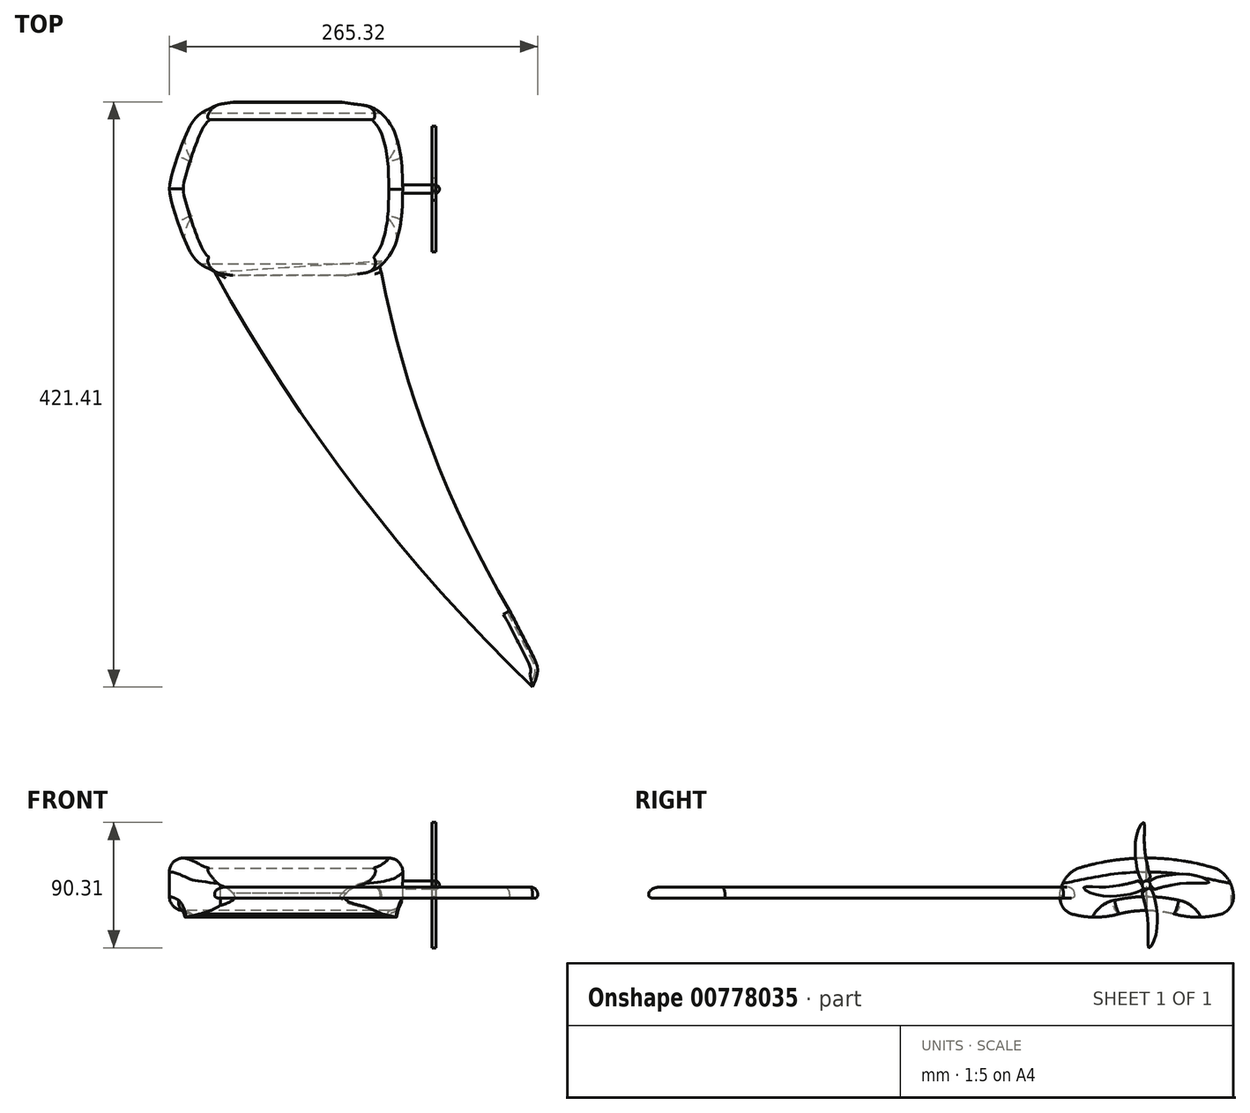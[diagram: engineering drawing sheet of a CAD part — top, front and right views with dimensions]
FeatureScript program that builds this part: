
annotation { "Feature Type Name" : "Feature", "Feature Type Description" : "" }
export const myFeature = defineFeature(function(context is Context, id is Id, definition is map)
    precondition{}
    {
        {
            var Q0;
            Q0=qCreatedBy(makeId("Right.planeOp"),FACE);
            var sketch = newSketch(context, id + "F0", { "sketchPlane" : qUnion([Q0])});
            skArc(sketch, "E0", {"start": v(50, -7.54) * mm, "mid": v(0, 0.01) * mm, "end": v(-50, -7.54) * mm});
            skArc(sketch, "E1", {"start": v(-50, -7.54) * mm, "mid": v(-58.49, -14.8) * mm, "end": v(-62.37, -25.27) * mm});
            skArc(sketch, "E2", {"start": v(-62.37, -25.27) * mm, "mid": v(-61.02, -34.16) * mm, "end": v(-54.32, -40.16) * mm});
            skArc(sketch, "E3", {"start": v(-54.32, -40.16) * mm, "mid": v(-36.95, -42.59) * mm, "end": v(-19.58, -40.16) * mm});
            skArc(sketch, "E4.MirrorCS", {"start": v(54.33, -40.16) * mm, "mid": v(36.96, -42.6) * mm, "end": v(19.6, -40.16) * mm});
            skArc(sketch, "E5.MirrorCS", {"start": v(62.37, -25.28) * mm, "mid": v(61.03, -34.17) * mm, "end": v(54.33, -40.16) * mm});
            skArc(sketch, "E6.MirrorCS", {"start": v(50, -7.55) * mm, "mid": v(58.5, -14.8) * mm, "end": v(62.37, -25.28) * mm});
            skFitSpline(sketch, "E7", {"points": [v(50, -7.55) * mm, v(50, -7.54) * mm], "startDerivative": vector(0, 0) * mm, "endDerivative": vector(0, 0) * mm});
            skArc(sketch, "E8", {"start": v(19.6, -40.16) * mm, "mid": v(0, -37.76) * mm, "end": v(-19.58, -40.16) * mm});
            skSolve(sketch);
        }
        {
            var Q0;
            Q0 = qSketchRegion(id + "F0", true);
            extrude(context, id + "F1", {"entities" : qUnion([Q0]), "depth" : 200 * mm, "offsetDistance" : 25 * mm});
        }
        {
            var Q0;
            Q0=qCreatedBy(makeId("Top.planeOp"),FACE);
            var sketch = newSketch(context, id + "F2", { "sketchPlane" : qUnion([Q0])});
            skFitSpline(sketch, "E9", {"points": [v(40.59, -61.05) * mm, v(32.26, -57.57) * mm, v(26.13, -54.16) * mm, v(20.46, -48.17) * mm, v(16.4, -40.56) * mm, v(11.23, -27.6) * mm, v(7.18, -15.78) * mm, v(3.78, 0) * mm], "startDerivative": vector(-74.7, 20.3) * mm, "endDerivative": vector(-2.34, 92.01) * mm});
            skFitSpline(sketch, "E10", {"points": [v(40.59, -61.05) * mm, v(44.6, -61.62) * mm, v(50.35, -62.52) * mm, v(55.66, -63.27) * mm], "startDerivative": vector(14.16, -1.62) * mm, "endDerivative": vector(15.47, -2.1) * mm});
            skFitSpline(sketch, "E11.MirrorCS", {"points": [v(40.59, 61.05) * mm, v(44.6, 61.62) * mm, v(50.35, 62.52) * mm, v(55.66, 63.27) * mm], "startDerivative": vector(14.16, 1.62) * mm, "endDerivative": vector(15.47, 2.1) * mm});
            skFitSpline(sketch, "E12", {"points": [v(139.37, 60.82) * mm, v(146.45, 59.7) * mm, v(152.68, 57.14) * mm, v(157.64, 53.32) * mm, v(162.03, 47.94) * mm, v(165.29, 42.55) * mm, v(168.26, 34.2) * mm, v(170.1, 25.98) * mm, v(171.23, 17.63) * mm, v(171.66, 9.98) * mm, v(171.94, -0.22) * mm], "startDerivative": vector(74.25, -8.33) * mm, "endDerivative": vector(2.34, -92.01) * mm});
            skFitSpline(sketch, "E13", {"points": [v(139.37, 60.82) * mm, v(134.8, 61.4) * mm, v(129.04, 62.3) * mm, v(123.73, 63.05) * mm], "startDerivative": vector(-14.16, 1.62) * mm, "endDerivative": vector(-15.47, 2.1) * mm});
            skFitSpline(sketch, "E14.MirrorCS", {"points": [v(139.37, -61.27) * mm, v(146.45, -60.14) * mm, v(152.68, -57.59) * mm, v(157.64, -53.76) * mm, v(162.03, -48.38) * mm, v(165.29, -43) * mm, v(168.26, -34.64) * mm, v(170.1, -26.43) * mm, v(171.23, -18.07) * mm, v(171.66, -10.42) * mm, v(171.94, -0.22) * mm], "startDerivative": vector(74.25, 8.33) * mm, "endDerivative": vector(2.34, 92.01) * mm});
            skFitSpline(sketch, "E15.MirrorCS", {"points": [v(139.37, -61.27) * mm, v(134.8, -61.84) * mm, v(129.04, -62.74) * mm, v(123.73, -63.5) * mm], "startDerivative": vector(-14.16, -1.62) * mm, "endDerivative": vector(-15.47, -2.1) * mm});
            skLineSegment(sketch, "E16", {"start": v(149.22, -63.5) * mm, "end": v(166.17, -79.7) * mm});
            skLineSegment(sketch, "E17", {"start": v(166.17, -79.7) * mm, "end": v(210.3, -72.3) * mm});
            skLineSegment(sketch, "E18", {"start": v(210.3, -72.3) * mm, "end": v(219.4, 8.55) * mm});
            skLineSegment(sketch, "E19", {"start": v(219.4, 8.55) * mm, "end": v(210.3, 73.23) * mm});
            skLineSegment(sketch, "E20", {"start": v(210.3, 73.23) * mm, "end": v(164.49, 80.64) * mm});
            skLineSegment(sketch, "E21", {"start": v(149.22, 63.05) * mm, "end": v(164.49, 80.64) * mm});
            skLineSegment(sketch, "E22", {"start": v(55.66, 63.27) * mm, "end": v(33.8, 74.16) * mm});
            skLineSegment(sketch, "E23", {"start": v(33.8, 74.16) * mm, "end": v(-5.06, 70.36) * mm});
            skLineSegment(sketch, "E24", {"start": v(-5.06, 70.36) * mm, "end": v(-13.47, 35.5) * mm});
            skLineSegment(sketch, "E25", {"start": v(-13.47, 35.5) * mm, "end": v(-13.27, -25.39) * mm});
            skLineSegment(sketch, "E26", {"start": v(-13.27, -25.39) * mm, "end": v(-7.26, -54.23) * mm});
            skLineSegment(sketch, "E27", {"start": v(-7.26, -54.23) * mm, "end": v(-1.45, -73.86) * mm});
            skLineSegment(sketch, "E28", {"start": v(-1.45, -73.86) * mm, "end": v(53.23, -68.45) * mm});
            skLineSegment(sketch, "E29", {"start": v(53.23, -68.45) * mm, "end": v(55.66, -63.27) * mm});
            skFitSpline(sketch, "E30.MirrorCS", {"points": [v(40.59, 61.05) * mm, v(32.26, 57.57) * mm, v(26.13, 54.16) * mm, v(20.46, 48.17) * mm, v(16.4, 40.56) * mm, v(11.23, 27.6) * mm, v(7.18, 15.78) * mm, v(3.78, 0) * mm], "startDerivative": vector(-74.7, -20.3) * mm, "endDerivative": vector(-2.34, -92.01) * mm});
            skLineSegment(sketch, "E31", {"start": v(149.22, -63.5) * mm, "end": v(123.73, -63.5) * mm});
            skLineSegment(sketch, "E32", {"start": v(123.73, 63.05) * mm, "end": v(149.22, 63.05) * mm});
            skSolve(sketch);
        }
        {
            var Q0;
            Q0=makeQuery(id+"F2.imprint","IMPRINT",FACE,{"disambiguationData":[TD([[makeQuery(id+"F2.imprint","IMPRINT",EDGE,{"derivedFrom":sQuery(id+"F2.wireOp",EDGE,"E9")}),1.0]])]});
            var Q1;
            Q1=makeQuery(id+"F2.imprint","IMPRINT",FACE,{"disambiguationData":[TD([[makeQuery(id+"F2.imprint","IMPRINT",EDGE,{"derivedFrom":sQuery(id+"F2.wireOp",EDGE,"E12")}),1.0]])]});
            extrude(context, id + "F3", {"entities" : qUnion([Q0, Q1]), "operationType" : NewBodyOperationType.REMOVE, "oppositeDirection" : true, "depth" : 74 * mm, "offsetDistance" : 25 * mm});
        }
        {
            var Q0;
            Q0=makeQuery(id+"F1.opExtrude","SWEPT_FACE",FACE,{"disambiguationData":[OSD([sQuery(id+"F0.wireOp",EDGE,"E0")])]});
            var Q1;
            Q1=makeQuery(id+"F1.opExtrude","SWEPT_FACE",FACE,{"disambiguationData":[OSD([sQuery(id+"F0.wireOp",EDGE,"E8")])]});
            fillet(context, id + "F4", {"entities" : qUnion([Q0, Q1]), "radius" : 10 * mm, "tangentPropagation" : true, "allowEdgeOverflow" : false});
        }
        {
            var Q0;
            Q0=qCreatedBy(makeId("Top.planeOp"),FACE);
            var sketch = newSketch(context, id + "F5", { "sketchPlane" : qUnion([Q0])});
            skArc(sketch, "E33", {"start": v(23.4, -59.92) * mm, "mid": v(126.63, -218) * mm, "end": v(252.43, -358.78) * mm});
            skArc(sketch, "E34", {"start": v(143.47, -59.92) * mm, "mid": v(179.26, -185.83) * mm, "end": v(235.94, -303.81) * mm});
            skFitSpline(sketch, "E35", {"points": [v(235.94, -303.81) * mm, v(251.98, -334.96) * mm, v(256.1, -346.87) * mm, v(252.43, -358.78) * mm], "startDerivative": vector(39.46, -76.57) * mm, "endDerivative": vector(-19.99, -45.14) * mm});
            skArc(sketch, "E36.MirrorCS", {"start": v(23.4, 59.92) * mm, "mid": v(126.63, 218) * mm, "end": v(252.43, 358.78) * mm});
            skArc(sketch, "E37.MirrorCS", {"start": v(143.47, 59.92) * mm, "mid": v(179.26, 185.83) * mm, "end": v(235.94, 303.81) * mm});
            skFitSpline(sketch, "E38.MirrorCS", {"points": [v(235.94, 303.81) * mm, v(251.98, 334.96) * mm, v(256.1, 346.87) * mm, v(252.43, 358.78) * mm], "startDerivative": vector(39.46, 76.57) * mm, "endDerivative": vector(-19.99, 45.14) * mm});
            skArc(sketch, "E39", {"start": v(143.47, -51.87) * mm, "mid": v(142.63, -55.9) * mm, "end": v(143.47, -59.92) * mm});
            skLineSegment(sketch, "E40", {"start": v(23.4, -59.92) * mm, "end": v(143.47, -51.87) * mm});
            skLineSegment(sketch, "E41.MirrorCS", {"start": v(23.4, 59.92) * mm, "end": v(143.47, 51.87) * mm});
            skArc(sketch, "E42.MirrorCS", {"start": v(143.47, 51.87) * mm, "mid": v(142.63, 55.9) * mm, "end": v(143.47, 59.92) * mm});
            skSolve(sketch);
        }
        {
            var Q0;
            Q0=makeQuery(id+"F5.imprint","IMPRINT",FACE,{"disambiguationData":[TD([[makeQuery(id+"F5.imprint","IMPRINT",EDGE,{"derivedFrom":sQuery(id+"F5.wireOp",EDGE,"E33")}),1.0]])]});
            var Q1;
            Q1=makeQuery(id+"F5.imprint","IMPRINT",FACE,{"disambiguationData":[TD([[makeQuery(id+"F5.imprint","IMPRINT",EDGE,{"derivedFrom":sQuery(id+"F5.wireOp",EDGE,"E36.MirrorCS")}),-1.0]])]});
            extrude(context, id + "F6", {"entities" : qUnion([Q0, Q1]), "depth" : 8 * mm, "offsetDistance" : 25 * mm});
        }
        {
            var Q0;
            Q0=makeQuery(id+"F6.opExtrude","CAP_FACE",FACE,{"disambiguationData":[OSD([sQuery(id+"F5.wireOp",EDGE,"6FdpHKt3-hqUe-cJeI-kYoZ-nh7BHDurZMUy"),sQuery(id+"F5.wireOp",EDGE,"E33"),sQuery(id+"F5.wireOp",EDGE,"E34"),sQuery(id+"F5.wireOp",EDGE,"E35")])],"isStart":false});
            var Q1;
            Q1=makeQuery(id+"F6.opExtrude","CAP_FACE",FACE,{"disambiguationData":[OSD([sQuery(id+"F5.wireOp",EDGE,"E36.MirrorCS"),sQuery(id+"F5.wireOp",EDGE,"b9c2965b-7b99-427b-b453-79c65aef091a0.MirrorCS"),sQuery(id+"F5.wireOp",EDGE,"E37.MirrorCS"),sQuery(id+"F5.wireOp",EDGE,"E38.MirrorCS")])],"isStart":false});
            fillet(context, id + "F7", {"entities" : qUnion([Q0, Q1]), "radius" : 5 * mm, "tangentPropagation" : true, "allowEdgeOverflow" : false});
        }
        {
            var Q0;
            Q0=makeQuery(id+"F6.opExtrude","CAP_FACE",FACE,{"disambiguationData":[OSD([sQuery(id+"F5.wireOp",EDGE,"E36.MirrorCS"),sQuery(id+"F5.wireOp",EDGE,"b9c2965b-7b99-427b-b453-79c65aef091a0.MirrorCS"),sQuery(id+"F5.wireOp",EDGE,"E37.MirrorCS"),sQuery(id+"F5.wireOp",EDGE,"E38.MirrorCS")])],"isStart":true});
            var Q1;
            Q1=makeQuery(id+"F6.opExtrude","CAP_FACE",FACE,{"disambiguationData":[OSD([sQuery(id+"F5.wireOp",EDGE,"6FdpHKt3-hqUe-cJeI-kYoZ-nh7BHDurZMUy"),sQuery(id+"F5.wireOp",EDGE,"E33"),sQuery(id+"F5.wireOp",EDGE,"E34"),sQuery(id+"F5.wireOp",EDGE,"E35")])],"isStart":true});
            fillet(context, id + "F8", {"entities" : qUnion([Q0, Q1]), "radius" : 2 * mm, "tangentPropagation" : true, "allowEdgeOverflow" : false});
        }
        {
            var Q0;
            Q0=makeQuery(id+"F6.opExtrude","SWEPT_BODY",BODY,{"disambiguationData":[OSD([sQuery(id+"F5.wireOp",EDGE,"6FdpHKt3-hqUe-cJeI-kYoZ-nh7BHDurZMUy"),sQuery(id+"F5.wireOp",EDGE,"E33"),sQuery(id+"F5.wireOp",EDGE,"E34"),sQuery(id+"F5.wireOp",EDGE,"E35")])]});
            var Q1;
            Q1=makeQuery(id+"F6.opExtrude","SWEPT_BODY",BODY,{"disambiguationData":[OSD([sQuery(id+"F5.wireOp",EDGE,"E36.MirrorCS"),sQuery(id+"F5.wireOp",EDGE,"b9c2965b-7b99-427b-b453-79c65aef091a0.MirrorCS"),sQuery(id+"F5.wireOp",EDGE,"E37.MirrorCS"),sQuery(id+"F5.wireOp",EDGE,"E38.MirrorCS")])]});
            transform(context, id + "F9", {"entities" : qUnion([Q0, Q1]), "transformType" : TransformType.TRANSLATION_3D, "dx" : 13 * mm, "dy" : 0 * mm, "dz" : -28.9 * mm, "makeCopy" : false});
        }
        {
            var Q0;
            Q0=qCreatedBy(makeId("Right.planeOp"),FACE);
            cPlane(context, id + "F10", {"entities" : qUnion([Q0]), "cplaneType" : CPlaneType.OFFSET, "offset" : 168 * mm, "width" : 150 * mm, "height" : 150 * mm});
        }
        {
            var Q0;
            Q0=qCreatedBy(id+"F10.planeOp",FACE);
            var sketch = newSketch(context, id + "F11", { "sketchPlane" : qUnion([Q0])});
            skCircle(sketch, "E43", {"center": v(-0.22, -19.44) * mm, "radius": 3 * mm});
            skSolve(sketch);
        }
        {
            var Q0;
            Q0 = qSketchRegion(id + "F11", true);
            extrude(context, id + "F12", {"entities" : qUnion([Q0]), "operationType" : NewBodyOperationType.ADD, "depth" : 25 * mm, "offsetDistance" : 25 * mm});
        }
        {
            var Q0;
            Q0=makeQuery(id+"F12.opExtrude","CAP_FACE",FACE,{"disambiguationData":[OSD([sQuery(id+"F11.wireOp",EDGE,"E43")])],"isStart":false});
            var sketch = newSketch(context, id + "F13", { "sketchPlane" : qUnion([Q0])});
            skFitSpline(sketch, "E44", {"points": [v(-0.22, -19.44) * mm, v(-1.67, -18.28) * mm, v(-4.67, -14.6) * mm, v(-7.33, -4.43) * mm, v(-8.14, 9.97) * mm, v(-5.07, 22.27) * mm, v(-2.16, 25.66) * mm, v(-1.51, 19.84) * mm, v(-1.35, 5.6) * mm, v(0.81, -6.27) * mm, v(2.07, -11.18) * mm, v(2.53, -14.39) * mm, v(0, -16.45) * mm, v(-0.22, -19.44) * mm]});
            skFitSpline(sketch, "E45", {"points": [v(-0.18, -19.51) * mm, v(1, -18.06) * mm, v(4.66, -15.07) * mm, v(14.84, -12.4) * mm, v(29.24, -11.6) * mm, v(41.53, -14.67) * mm, v(44.93, -17.58) * mm, v(39.1, -18.23) * mm, v(24.87, -18.39) * mm, v(13, -20.55) * mm, v(8.08, -21.81) * mm, v(4.88, -22.27) * mm, v(2.81, -19.74) * mm, v(-0.18, -19.51) * mm]});
            skFitSpline(sketch, "E46", {"points": [v(-0.23, -19.5) * mm, v(1.22, -20.67) * mm, v(4.2, -24.34) * mm, v(6.88, -34.52) * mm, v(7.69, -48.92) * mm, v(4.61, -61.21) * mm, v(1.7, -64.61) * mm, v(1.05, -58.79) * mm, v(0.9, -44.55) * mm, v(-1.27, -32.68) * mm, v(-2.53, -27.76) * mm, v(-2.99, -24.56) * mm, v(-0.46, -22.5) * mm, v(-0.23, -19.5) * mm]});
            skFitSpline(sketch, "E47", {"points": [v(-0.28, -19.43) * mm, v(-1.45, -20.88) * mm, v(-5.12, -23.88) * mm, v(-15.3, -26.55) * mm, v(-29.7, -27.36) * mm, v(-41.99, -24.28) * mm, v(-45.39, -21.37) * mm, v(-39.56, -20.72) * mm, v(-25.33, -20.56) * mm, v(-13.46, -18.4) * mm, v(-8.54, -17.14) * mm, v(-5.34, -16.68) * mm, v(-3.27, -19.21) * mm, v(-0.28, -19.43) * mm]});
            skSolve(sketch);
        }
        {
            var Q0;
            Q0 = qSketchRegion(id + "F13", true);
            extrude(context, id + "F14", {"entities" : qUnion([Q0]), "operationType" : NewBodyOperationType.ADD, "depth" : 3 * mm, "offsetDistance" : 25 * mm});
        }
        {
            var Q0;
            Q0 = qSketchRegion(id + "F11", true);
            extrude(context, id + "F15", {"entities" : qUnion([Q0]), "operationType" : NewBodyOperationType.ADD, "depth" : 30.4 * mm, "offsetDistance" : 25 * mm});
        }
        {
            var Q0;
            Q0=makeQuery(id+"F15.opExtrude","CAP_FACE",FACE,{"disambiguationData":[OSD([sQuery(id+"F11.wireOp",EDGE,"E43")])],"isStart":false});
            fillet(context, id + "F16", {"entities" : qUnion([Q0]), "radius" : 3 * mm, "tangentPropagation" : true, "allowEdgeOverflow" : false});
        }
    });
